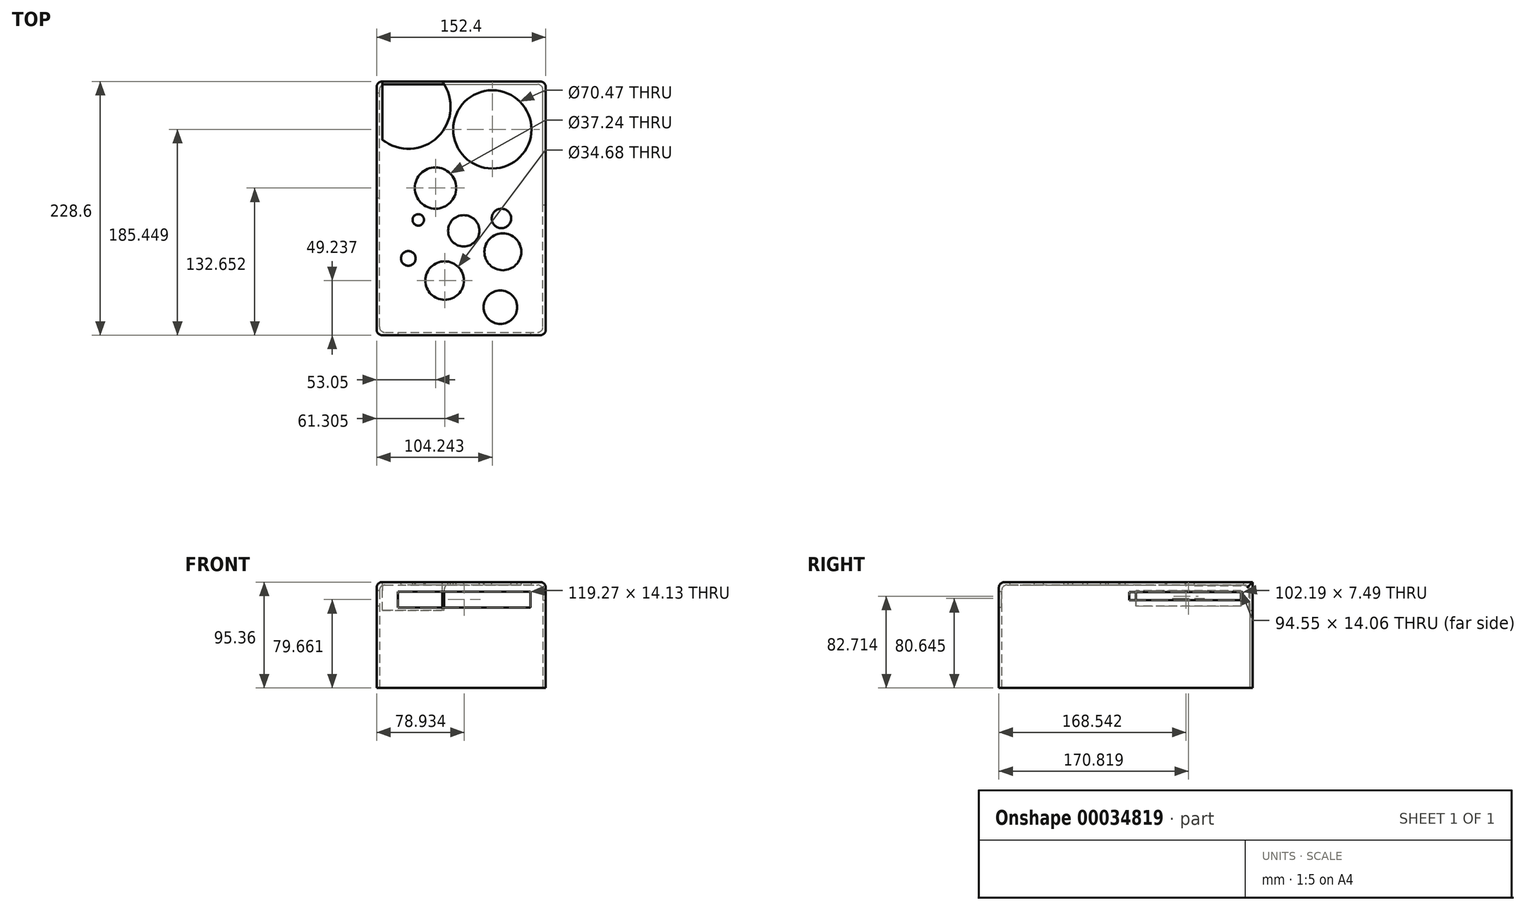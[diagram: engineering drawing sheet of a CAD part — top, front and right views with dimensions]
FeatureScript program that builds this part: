
annotation { "Feature Type Name" : "Feature", "Feature Type Description" : "" }
export const myFeature = defineFeature(function(context is Context, id is Id, definition is map)
    precondition{}
    {
        {
            var Q0;
            Q0=qCreatedBy(makeId("Front.planeOp"),FACE);
            var sketch = newSketch(context, id + "F0", { "sketchPlane" : qUnion([Q0])});
            skLineSegment(sketch, "E0.bottom", {"start": v(-117.34, 62.42) * mm, "end": v(35.06, 62.42) * mm});
            skLineSegment(sketch, "E0.top", {"start": v(-117.34, -32.94) * mm, "end": v(35.06, -32.94) * mm});
            skLineSegment(sketch, "E0.left", {"start": v(-117.34, 62.42) * mm, "end": v(-117.34, -32.94) * mm});
            skLineSegment(sketch, "E0.right", {"start": v(35.06, 62.42) * mm, "end": v(35.06, -32.94) * mm});
            skSolve(sketch);
        }
        {
            var Q0;
            Q0=makeQuery(id+"F0.imprint","IMPRINT",FACE,{"disambiguationData":[TD([[makeQuery(id+"F0.imprint","IMPRINT",EDGE,{"derivedFrom":sQuery(id+"F0.wireOp",EDGE,"E0.bottom")}),-1.0]])]});
            extrude(context, id + "F1", {"entities" : qUnion([Q0]), "depth" : 228.6 * mm});
        }
        {
            var Q0;
            Q0=makeQuery(id+"F1.opExtrude","SWEPT_FACE",FACE,{"disambiguationData":[OSD([sQuery(id+"F0.wireOp",EDGE,"E0.top")])]});
            shell(context, id + "F2", {"entities" : qUnion([Q0]), "thickness" : 2.54 * mm});
        }
        {
            var Q0;
            Q0=makeQuery(id+"F2.opShell","OFFSET_EDGE",EDGE,{"disambiguationData":[OSD([sQuery(id+"F0.wireOp",EDGE,"E0.bottom"),sQuery(id+"F0.wireOp",EDGE,"E0.left")])]});
            var Q1;
            {var subQ0=sQuery(id+"F0.wireOp",EDGE,"E0.left");Q1=makeQuery(id+"F2.opShell","OFFSET_EDGE",EDGE,{"disambiguationData":[OSD([subQ0]),TDD([makeQuery(id+"F1.opExtrude","CAP_EDGE",EDGE,{"disambiguationData":[OSD([subQ0])],"isStart":false})])]});}
            var Q2;
            {var subQ0=sQuery(id+"F0.wireOp",EDGE,"E0.bottom");Q2=makeQuery(id+"F2.opShell","OFFSET_EDGE",EDGE,{"disambiguationData":[OSD([subQ0]),TDD([makeQuery(id+"F1.opExtrude","CAP_EDGE",EDGE,{"disambiguationData":[OSD([subQ0])],"isStart":false})])]});}
            var Q3;
            {var subQ0=sQuery(id+"F0.wireOp",EDGE,"E0.right");Q3=makeQuery(id+"F2.opShell","OFFSET_EDGE",EDGE,{"disambiguationData":[OSD([subQ0]),TDD([makeQuery(id+"F1.opExtrude","CAP_EDGE",EDGE,{"disambiguationData":[OSD([subQ0])],"isStart":false})])]});}
            var Q4;
            {var subQ0=sQuery(id+"F0.wireOp",EDGE,"E0.bottom");Q4=makeQuery(id+"F2.opShell","OFFSET_EDGE",EDGE,{"disambiguationData":[OSD([subQ0]),TDD([makeQuery(id+"F1.opExtrude","CAP_EDGE",EDGE,{"disambiguationData":[OSD([subQ0])],"isStart":true})])]});}
            var Q5;
            {var subQ0=sQuery(id+"F0.wireOp",EDGE,"E0.left");Q5=makeQuery(id+"F2.opShell","OFFSET_EDGE",EDGE,{"disambiguationData":[OSD([subQ0]),TDD([makeQuery(id+"F1.opExtrude","CAP_EDGE",EDGE,{"disambiguationData":[OSD([subQ0])],"isStart":true})])]});}
            var Q6;
            Q6=makeQuery(id+"F1.opExtrude","CAP_EDGE",EDGE,{"disambiguationData":[OSD([sQuery(id+"F0.wireOp",EDGE,"E0.right")])],"isStart":true});
            var Q7;
            Q7=makeQuery(id+"F1.opExtrude","CAP_EDGE",EDGE,{"disambiguationData":[OSD([sQuery(id+"F0.wireOp",EDGE,"E0.left")])],"isStart":true});
            var Q8;
            Q8=makeQuery(id+"F1.opExtrude","CAP_EDGE",EDGE,{"disambiguationData":[OSD([sQuery(id+"F0.wireOp",EDGE,"E0.left")])],"isStart":false});
            var Q9;
            Q9=makeQuery(id+"F1.opExtrude","CAP_EDGE",EDGE,{"disambiguationData":[OSD([sQuery(id+"F0.wireOp",EDGE,"E0.right")])],"isStart":false});
            var Q10;
            {var subQ0=sQuery(id+"F0.wireOp",EDGE,"E0.right");Q10=makeQuery(id+"F2.opShell","OFFSET_EDGE",EDGE,{"disambiguationData":[OSD([subQ0]),TDD([makeQuery(id+"F1.opExtrude","CAP_EDGE",EDGE,{"disambiguationData":[OSD([subQ0])],"isStart":true})])]});}
            var Q11;
            Q11=makeQuery(id+"F1.opExtrude","SWEPT_EDGE",EDGE,{"disambiguationData":[OSD([sQuery(id+"F0.wireOp",EDGE,"E0.bottom"),sQuery(id+"F0.wireOp",EDGE,"E0.right")])]});
            var Q12;
            Q12=makeQuery(id+"F1.opExtrude","CAP_EDGE",EDGE,{"disambiguationData":[OSD([sQuery(id+"F0.wireOp",EDGE,"E0.bottom")])],"isStart":false});
            var Q13;
            Q13=makeQuery(id+"F1.opExtrude","SWEPT_EDGE",EDGE,{"disambiguationData":[OSD([sQuery(id+"F0.wireOp",EDGE,"E0.bottom"),sQuery(id+"F0.wireOp",EDGE,"E0.left")])]});
            var Q14;
            Q14=makeQuery(id+"F2.opShell","OFFSET_FACE",FACE,{"disambiguationData":[OSD([sQuery(id+"F0.wireOp",EDGE,"E0.bottom")])]});
            fillet(context, id + "F3", {"entities" : qUnion([Q0, Q1, Q2, Q3, Q4, Q5, Q6, Q7, Q8, Q9, Q10, Q11, Q12, Q13, Q14]), "radius" : 5.08 * mm, "tangentPropagation" : true, "allowEdgeOverflow" : false});
        }
        {
            var Q0;
            Q0=makeQuery(id+"F1.opExtrude","SWEPT_FACE",FACE,{"disambiguationData":[OSD([sQuery(id+"F0.wireOp",EDGE,"E0.bottom")])]});
            var sketch = newSketch(context, id + "F4", { "sketchPlane" : qUnion([Q0])});
            skCircle(sketch, "E1", {"center": v(-13.1, -43.15) * mm, "radius": 35.24 * mm});
            skSolve(sketch);
        }
        {
            var Q0;
            Q0 = qSketchRegion(id + "F4", true);
            extrude(context, id + "F5", {"entities" : qUnion([Q0]), "operationType" : NewBodyOperationType.REMOVE, "oppositeDirection" : true, "depth" : 25.4 * mm});
        }
        {
            var Q0;
            Q0=makeQuery(id+"F1.opExtrude","SWEPT_FACE",FACE,{"disambiguationData":[OSD([sQuery(id+"F0.wireOp",EDGE,"E0.bottom")])]});
            var sketch = newSketch(context, id + "F6", { "sketchPlane" : qUnion([Q0])});
            skCircle(sketch, "E2", {"center": v(-3.65, -153.46) * mm, "radius": 16.57 * mm});
            skCircle(sketch, "E3", {"center": v(-64.3, -95.95) * mm, "radius": 18.62 * mm});
            skCircle(sketch, "E4", {"center": v(-56.04, -179.36) * mm, "radius": 17.34 * mm});
            skCircle(sketch, "E5", {"center": v(-4.9, -123.4) * mm, "radius": 8.74 * mm});
            skCircle(sketch, "E6", {"center": v(-88.62, -22.68) * mm, "radius": 37.94 * mm});
            skSolve(sketch);
        }
        {
            var Q0;
            {var subQ0=sQuery(id+"F0.wireOp",EDGE,"E0.bottom");var subQ1=makeQuery(id+"F1.opExtrude","CAP_EDGE",EDGE,{"disambiguationData":[OSD([subQ0])],"isStart":true});var subQ2=sQuery(id+"F6.wireOp",EDGE,"E6");var subQ3=makeQuery(id+"F6.imprint","INTERSECT",VERTEX,{"derivedFrom":[subQ1,subQ2]});Q0=makeQuery(id+"F6.imprint","IMPRINT",FACE,{"disambiguationData":[TD([[makeQuery(id+"F6.imprint","IMPRINT",EDGE,{"disambiguationData":[TD([[subQ3,1.0]])],"derivedFrom":subQ2}),1.0]])]});}
            var Q1;
            Q1=makeQuery(id+"F6.imprint","IMPRINT",FACE,{"disambiguationData":[TD([[makeQuery(id+"F6.imprint","IMPRINT",EDGE,{"derivedFrom":sQuery(id+"F6.wireOp",EDGE,"E3")}),1.0]])]});
            var Q2;
            Q2=makeQuery(id+"F6.imprint","IMPRINT",FACE,{"disambiguationData":[TD([[makeQuery(id+"F6.imprint","IMPRINT",EDGE,{"derivedFrom":sQuery(id+"F6.wireOp",EDGE,"E2")}),1.0]])]});
            var Q3;
            Q3=makeQuery(id+"F6.imprint","IMPRINT",FACE,{"disambiguationData":[TD([[makeQuery(id+"F6.imprint","IMPRINT",EDGE,{"derivedFrom":sQuery(id+"F6.wireOp",EDGE,"E5")}),1.0]])]});
            var Q4;
            Q4=makeQuery(id+"F6.imprint","IMPRINT",FACE,{"disambiguationData":[TD([[makeQuery(id+"F6.imprint","IMPRINT",EDGE,{"derivedFrom":sQuery(id+"F6.wireOp",EDGE,"E4")}),1.0]])]});
            extrude(context, id + "F7", {"entities" : qUnion([Q0, Q1, Q2, Q3, Q4]), "operationType" : NewBodyOperationType.REMOVE, "oppositeDirection" : true, "depth" : 25.4 * mm});
        }
        {
            var Q0;
            Q0=makeQuery(id+"F1.opExtrude","SWEPT_FACE",FACE,{"disambiguationData":[OSD([sQuery(id+"F0.wireOp",EDGE,"E0.bottom")])]});
            var sketch = newSketch(context, id + "F8", { "sketchPlane" : qUnion([Q0])});
            skCircle(sketch, "E7", {"center": v(-79.74, -124.66) * mm, "radius": 5.14 * mm});
            skCircle(sketch, "E8", {"center": v(-5.85, -203.36) * mm, "radius": 15.15 * mm});
            skCircle(sketch, "E9", {"center": v(-88.78, -159.4) * mm, "radius": 6.62 * mm});
            skCircle(sketch, "E10", {"center": v(-38.86, -134.52) * mm, "radius": 14.1 * mm});
            skSolve(sketch);
        }
        {
            var Q0;
            Q0=makeQuery(id+"F8.imprint","IMPRINT",FACE,{"disambiguationData":[TD([[makeQuery(id+"F8.imprint","IMPRINT",EDGE,{"derivedFrom":sQuery(id+"F8.wireOp",EDGE,"E7")}),1.0]])]});
            var Q1;
            Q1=makeQuery(id+"F8.imprint","IMPRINT",FACE,{"disambiguationData":[TD([[makeQuery(id+"F8.imprint","IMPRINT",EDGE,{"derivedFrom":sQuery(id+"F8.wireOp",EDGE,"E10")}),1.0]])]});
            var Q2;
            Q2=makeQuery(id+"F8.imprint","IMPRINT",FACE,{"disambiguationData":[TD([[makeQuery(id+"F8.imprint","IMPRINT",EDGE,{"derivedFrom":sQuery(id+"F8.wireOp",EDGE,"E9")}),1.0]])]});
            var Q3;
            Q3=makeQuery(id+"F8.imprint","IMPRINT",FACE,{"disambiguationData":[TD([[makeQuery(id+"F8.imprint","IMPRINT",EDGE,{"derivedFrom":sQuery(id+"F8.wireOp",EDGE,"E8")}),1.0]])]});
            extrude(context, id + "F9", {"entities" : qUnion([Q0, Q1, Q2, Q3]), "operationType" : NewBodyOperationType.REMOVE, "oppositeDirection" : true, "depth" : 25.4 * mm});
        }
        {
            var Q0;
            Q0=makeQuery(id+"F1.opExtrude","CAP_FACE",FACE,{"disambiguationData":[OSD([sQuery(id+"F0.wireOp",EDGE,"E0.bottom"),sQuery(id+"F0.wireOp",EDGE,"E0.top"),sQuery(id+"F0.wireOp",EDGE,"E0.left"),sQuery(id+"F0.wireOp",EDGE,"E0.right")])],"isStart":false});
            var sketch = newSketch(context, id + "F10", { "sketchPlane" : qUnion([Q0])});
            skLineSegment(sketch, "E11.bottom", {"start": v(-98.04, 39.65) * mm, "end": v(21.23, 39.65) * mm});
            skLineSegment(sketch, "E11.top", {"start": v(-98.04, 53.79) * mm, "end": v(21.23, 53.79) * mm});
            skLineSegment(sketch, "E11.left", {"start": v(-98.04, 39.65) * mm, "end": v(-98.04, 53.79) * mm});
            skLineSegment(sketch, "E11.right", {"start": v(21.23, 39.65) * mm, "end": v(21.23, 53.79) * mm});
            skSolve(sketch);
        }
        {
            var Q0;
            Q0=makeQuery(id+"F10.imprint","IMPRINT",FACE,{"disambiguationData":[TD([[makeQuery(id+"F10.imprint","IMPRINT",EDGE,{"derivedFrom":sQuery(id+"F10.wireOp",EDGE,"E11.bottom")}),1.0]])]});
            extrude(context, id + "F11", {"entities" : qUnion([Q0]), "operationType" : NewBodyOperationType.REMOVE, "oppositeDirection" : true, "depth" : 25.4 * mm});
        }
        {
            var Q0;
            Q0=makeQuery(id+"F1.opExtrude","SWEPT_FACE",FACE,{"disambiguationData":[OSD([sQuery(id+"F0.wireOp",EDGE,"E0.left")])]});
            var sketch = newSketch(context, id + "F12", { "sketchPlane" : qUnion([Q0])});
            skLineSegment(sketch, "E12.bottom", {"start": v(10.5, 40.67) * mm, "end": v(105.06, 40.67) * mm});
            skLineSegment(sketch, "E12.top", {"start": v(10.5, 54.74) * mm, "end": v(105.06, 54.74) * mm});
            skLineSegment(sketch, "E12.left", {"start": v(10.5, 40.67) * mm, "end": v(10.5, 54.74) * mm});
            skLineSegment(sketch, "E12.right", {"start": v(105.06, 40.67) * mm, "end": v(105.06, 54.74) * mm});
            skSolve(sketch);
        }
        {
            var Q0;
            Q0=makeQuery(id+"F12.imprint","IMPRINT",FACE,{"disambiguationData":[TD([[makeQuery(id+"F12.imprint","IMPRINT",EDGE,{"derivedFrom":sQuery(id+"F12.wireOp",EDGE,"E12.bottom")}),1.0]])]});
            extrude(context, id + "F13", {"entities" : qUnion([Q0]), "operationType" : NewBodyOperationType.REMOVE, "oppositeDirection" : true, "depth" : 25.4 * mm});
        }
        {
            var Q0;
            Q0=makeQuery(id+"F1.opExtrude","SWEPT_FACE",FACE,{"disambiguationData":[OSD([sQuery(id+"F0.wireOp",EDGE,"E0.right")])]});
            var sketch = newSketch(context, id + "F14", { "sketchPlane" : qUnion([Q0])});
            skLineSegment(sketch, "E13.bottom", {"start": v(-111.15, 53.52) * mm, "end": v(-8.96, 53.52) * mm});
            skLineSegment(sketch, "E13.top", {"start": v(-111.15, 46.03) * mm, "end": v(-8.96, 46.03) * mm});
            skLineSegment(sketch, "E13.left", {"start": v(-111.15, 53.52) * mm, "end": v(-111.15, 46.03) * mm});
            skLineSegment(sketch, "E13.right", {"start": v(-8.96, 53.52) * mm, "end": v(-8.96, 46.03) * mm});
            skSolve(sketch);
        }
        {
            var Q0;
            Q0=makeQuery(id+"F14.imprint","IMPRINT",FACE,{"disambiguationData":[TD([[makeQuery(id+"F14.imprint","IMPRINT",EDGE,{"derivedFrom":sQuery(id+"F14.wireOp",EDGE,"E13.bottom")}),-1.0]])]});
            extrude(context, id + "F15", {"entities" : qUnion([Q0]), "operationType" : NewBodyOperationType.REMOVE, "oppositeDirection" : true, "depth" : 25.4 * mm});
        }
    });
